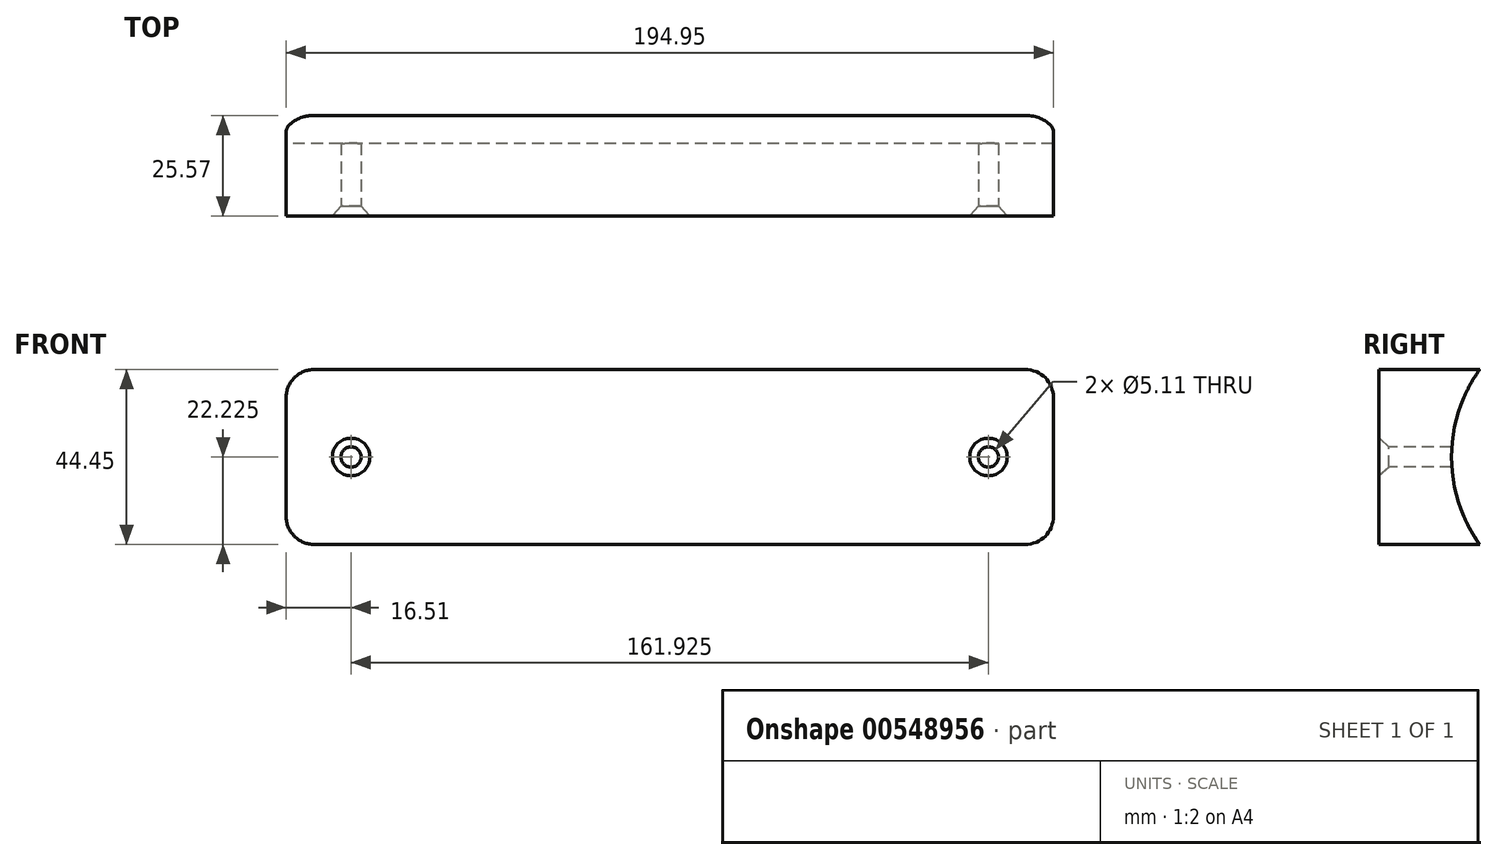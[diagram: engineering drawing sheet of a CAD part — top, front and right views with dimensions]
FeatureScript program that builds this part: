
annotation { "Feature Type Name" : "Feature", "Feature Type Description" : "" }
export const myFeature = defineFeature(function(context is Context, id is Id, definition is map)
    precondition{}
    {
        {
            var Q0;
            Q0=qCreatedBy(makeId("Front.planeOp"),FACE);
            var sketch = newSketch(context, id + "F0", { "sketchPlane" : qUnion([Q0])});
            skLineSegment(sketch, "E0", {"start": v(0, 0) * mm, "end": v(0, 44.45) * mm});
            skLineSegment(sketch, "E1", {"start": v(0, 44.45) * mm, "end": v(194.94, 44.45) * mm});
            skLineSegment(sketch, "E2", {"start": v(194.94, 44.45) * mm, "end": v(194.94, 0) * mm});
            skLineSegment(sketch, "E3", {"start": v(194.94, 0) * mm, "end": v(0, 0) * mm});
            skPoint(sketch, "E4", {"position": v(16.51, 22.23) * mm});
            skPoint(sketch, "E4.positionSnap0", {"position": v(0, 22.23) * mm});
            skPoint(sketch, "E5", {"position": v(178.44, 22.23) * mm});
            skSolve(sketch);
        }
        {
            var Q0;
            Q0=makeQuery(id+"F0.imprint","IMPRINT",FACE,{"disambiguationData":[TD([[makeQuery(id+"F0.imprint","IMPRINT",EDGE,{"derivedFrom":sQuery(id+"F0.wireOp",EDGE,"E0")}),-1.0]])]});
            extrude(context, id + "F1", {"entities" : qUnion([Q0]), "oppositeDirection" : true, "depth" : 40.64 * mm, "offsetDistance" : 25.4 * mm});
        }
        {
            var Q0;
            Q0=sQuery(id+"F0.wireOp",VERTEX,"E4");
            var Q1;
            Q1=sQuery(id+"F0.wireOp",VERTEX,"E5");
            var Q2;
            Q2=makeQuery(id+"F1.opExtrude","SWEPT_BODY",BODY,{"disambiguationData":[OSD([sQuery(id+"F0.wireOp",EDGE,"E0"),sQuery(id+"F0.wireOp",EDGE,"E1"),sQuery(id+"F0.wireOp",EDGE,"E2"),sQuery(id+"F0.wireOp",EDGE,"E3")])]});
            hole(context, id + "F2", {"style" : HoleStyle.C_SINK, "endStyle" : HoleEndStyle.BLIND, "holeDiameter" : 5.1 * mm, "cSinkDiameter" : 9.52 * mm, "cSinkAngle" : 82 * degree, "holeDepth" : 25.4 * mm, "isTappedThrough" : true, "tappedDepth" : 10.17 * mm, "tapClearance" : 3, "locations" : qUnion([Q0, Q1]), "scope" : qUnion([Q2])});
        }
        {
            var Q0;
            Q0=makeQuery(id+"F1.opExtrude","SWEPT_EDGE",EDGE,{"disambiguationData":[OSD([sQuery(id+"F0.wireOp",EDGE,"E0"),sQuery(id+"F0.wireOp",EDGE,"E1")])]});
            var Q1;
            Q1=makeQuery(id+"F1.opExtrude","SWEPT_EDGE",EDGE,{"disambiguationData":[OSD([sQuery(id+"F0.wireOp",EDGE,"E1"),sQuery(id+"F0.wireOp",EDGE,"E2")])]});
            var Q2;
            Q2=makeQuery(id+"F1.opExtrude","SWEPT_EDGE",EDGE,{"disambiguationData":[OSD([sQuery(id+"F0.wireOp",EDGE,"E0"),sQuery(id+"F0.wireOp",EDGE,"E3")])]});
            var Q3;
            Q3=makeQuery(id+"F1.opExtrude","SWEPT_EDGE",EDGE,{"disambiguationData":[OSD([sQuery(id+"F0.wireOp",EDGE,"E2"),sQuery(id+"F0.wireOp",EDGE,"E3")])]});
            fillet(context, id + "F3", {"entities" : qUnion([Q0, Q1, Q2, Q3]), "radius" : 7.14 * mm, "tangentPropagation" : true, "allowEdgeOverflow" : false});
        }
        {
            var Q0;
            Q0=makeQuery(id+"F1.opExtrude","SWEPT_FACE",FACE,{"disambiguationData":[OSD([sQuery(id+"F0.wireOp",EDGE,"E0")])]});
            var sketch = newSketch(context, id + "F4", { "sketchPlane" : qUnion([Q0])});
            skLineSegment(sketch, "E6", {"start": v(-40.64, 22.23) * mm, "end": v(0, 22.23) * mm});
            skCircle(sketch, "E7", {"center": v(-56.52, 22.23) * mm, "radius": 38.1 * mm});
            skSolve(sketch);
        }
        {
            var Q0;
            {var subQ0=sQuery(id+"F0.wireOp",EDGE,"E0");var subQ1=makeQuery(id+"F1.opExtrude","CAP_EDGE",EDGE,{"disambiguationData":[OSD([subQ0])],"isStart":false});var subQ5=makeQuery(id+"F4.imprint","INTERSECT",VERTEX,{"derivedFrom":[subQ1,sQuery(id+"F4.wireOp",EDGE,"E6")]});Q0=makeQuery(id+"F4.imprint","IMPRINT",FACE,{"disambiguationData":[TD([[makeQuery(id+"F4.imprint","IMPRINT",EDGE,{"disambiguationData":[TD([[subQ5,1.0]])],"derivedFrom":subQ1}),1.0]])]});}
            var Q1;
            {var subQ0=sQuery(id+"F4.wireOp",EDGE,"E6");var subQ1=sQuery(id+"F0.wireOp",EDGE,"E0");var subQ2=makeQuery(id+"F1.opExtrude","CAP_EDGE",EDGE,{"disambiguationData":[OSD([subQ1])],"isStart":false});var subQ3=makeQuery(id+"F4.imprint","INTERSECT",VERTEX,{"derivedFrom":[subQ2,subQ0]});Q1=makeQuery(id+"F4.imprint","IMPRINT",FACE,{"disambiguationData":[TD([[makeQuery(id+"F4.imprint","IMPRINT",EDGE,{"disambiguationData":[TD([[subQ3,-1.0]])],"derivedFrom":subQ0}),1.0]])]});}
            var Q2;
            {var subQ0=sQuery(id+"F4.wireOp",EDGE,"E6");var subQ1=sQuery(id+"F0.wireOp",EDGE,"E0");var subQ2=makeQuery(id+"F1.opExtrude","CAP_EDGE",EDGE,{"disambiguationData":[OSD([subQ1])],"isStart":false});var subQ3=makeQuery(id+"F4.imprint","INTERSECT",VERTEX,{"derivedFrom":[subQ2,subQ0]});Q2=makeQuery(id+"F4.imprint","IMPRINT",FACE,{"disambiguationData":[TD([[makeQuery(id+"F4.imprint","IMPRINT",EDGE,{"disambiguationData":[TD([[subQ3,-1.0]])],"derivedFrom":subQ0}),-1.0]])]});}
            extrude(context, id + "F5", {"entities" : qUnion([Q0, Q1, Q2]), "operationType" : NewBodyOperationType.REMOVE, "endBound" : BoundingType.THROUGH_ALL, "oppositeDirection" : true, "depth" : 25.4 * mm, "offsetDistance" : 25.4 * mm});
        }
    });
